# Revit family: Building-FlushMountingEnclosures-GEWISS-24SC-GREENWALL-BOXES_4P+4P
name_source: partatom
category: Apparecchi elettrici
revit_build: Autodesk Revit 2016 (Build: 20161004_0715(x64)
units: mm (PartAtom-declared; Revit-internal decimal feet)

## family parameters
Condiviso = Sì
Host = Superficie
Mantenere orientamento annotazione = Sì
Numero OmniClass = 23.80.30.14.24
Punto di calcolo locali = Sì
Quota connettore circolare = Usa diametro
Taglio con vuoti quando caricato = Sì
Tipo di parte = Normale
Titolo OmniClass = Junction Boxes

## types (1)
- GW24237PM - Halogen free - 8P (4+4)
    Catalogue = BUILDING
    Catalogue Range = 24SC
    Characteristics = Halogen free
    Compartment pre-arrangement = 2
    Description = Command panels
    Description: = 8 gang (4+4)
    Descrizione = 8 (4+4) GANG HIGH CAP.FLUSH M.GREEN BOX
    EAN code = 8011564801868
    Electrocod = 0110
    Fixing supports axles distance = 108,5MM
    For walls = Plasterboard
    Glow Wire Test = 850°C
    IDF = ea7f37d5-a322-4584-94c6-af8bec19da21
    IDT = 39fe7c71-9ec4-408e-b869-c61f51db61d8
    IP degree = IP40
    Immagine tipo = GW24237PM.jpg
    Installation = Flush mounting enclosures
    Modello = GW24237PM
    No. SYSTEM modules = 8 gang (4+4)
    Operating temperature = -15 ÷ +60°C
    Outer dim. LxHxD (mm) = 131x129x53
    Produttore = GEWISS S.p.A.
    Prospetto di default = 1219.2 mm  [stored 4 ft]
    SEO = Box
    Scatola = GEWISS - scatola a incasso
    Shock resistance = IK07
    Technical sheet = https://www.gewiss.com
    Thermo-pressure with ball = 70
    Type of material = Halogen free with Standard EN 50267-2-2
    Type: = High capacity
    URL = https://www.gewiss.com
    Version file RFA = 19.0

note: source unit labels omitted for Thermo-pressure with ball — the stored unit's dimension contradicts the parameter name (converter mislabeling)

note: [stored X ft] marks values corroborated as IEEE doubles in the binary element streams (Revit-internal decimal feet)

## geometry (parser evidence)
native form markers: Sweep x2
no freeform markers — native parametric forms only
